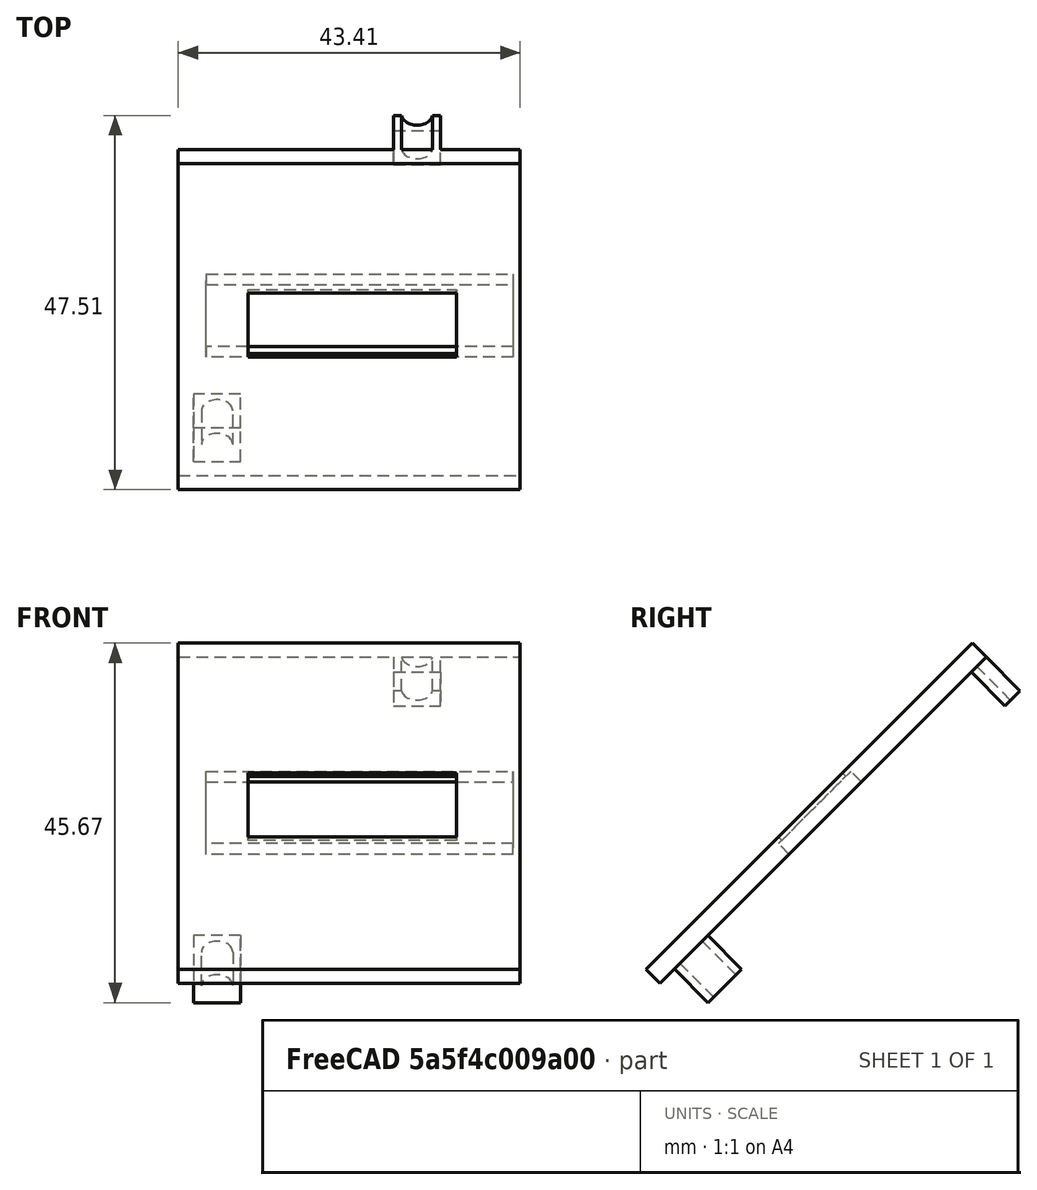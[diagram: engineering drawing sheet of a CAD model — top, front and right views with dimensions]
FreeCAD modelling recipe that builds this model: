
FCSTD DOCUMENT  (FreeCAD 0.20R29177 (Git))
Label: epreuvePcbFav
License: All rights reserved
LicenseURL: http://en.wikipedia.org/wiki/All_rights_reserved
objects: Part::Box×4, Part::Cut×4, Part::Feature×1
note: 9 computed .brp shape members not serialized (recipe doc carries the construction recipe); baked Part::Feature solids carry a one-line shape summary decoded from their .brp

FEATURE [Part::Feature] Part__Feature  label="faceAvant"
  shape: bbox 85 x 69.26 x 67.71 mm, 101 faces (baked)
FEATURE [Part::Box] Box  label="Cube"
  AttacherType = Attacher::AttachEngine3D
  Height = 23
  Length = 93
  Placement = pos=(1.47,-82.9012,14.227) rot=(0,0.92388,0.382683;3.14159rad)
  Width = 17
FEATURE [Part::Box] Box001  label="Cube001"
  AttacherType = Attacher::AttachEngine3D
  Height = 23
  Length = 93
  Placement = pos=(1.47,-29.4298,67.6984) rot=(0,0.92388,0.382683;3.14159rad)
  Width = 17
FEATURE [Part::Box] Box002  label="Cube002"
  AttacherType = Attacher::AttachEngine3D
  Height = 23
  Length = 38
  Placement = pos=(1.47,-73.6452,23.483) rot=(0,0.92388,0.382683;3.14159rad)
  Width = 68
FEATURE [Part::Box] Box003  label="Cube003"
  AttacherType = Attacher::AttachEngine3D
  Height = 24
  Length = 93
  Placement = pos=(-79.94,-72.3724,24.7558) rot=(0,0.92388,0.382683;3.14159rad)
  Width = 64
FEATURE [Part::Cut] Cut
  Base = -> Part__Feature
  Tool = -> Box
FEATURE [Part::Cut] Cut001
  Base = -> Cut
  Tool = -> Box001
FEATURE [Part::Cut] Cut002
  Base = -> Cut001
  Tool = -> Box002
FEATURE [Part::Cut] Cut003
  Base = -> Cut002
  Tool = -> Box003
